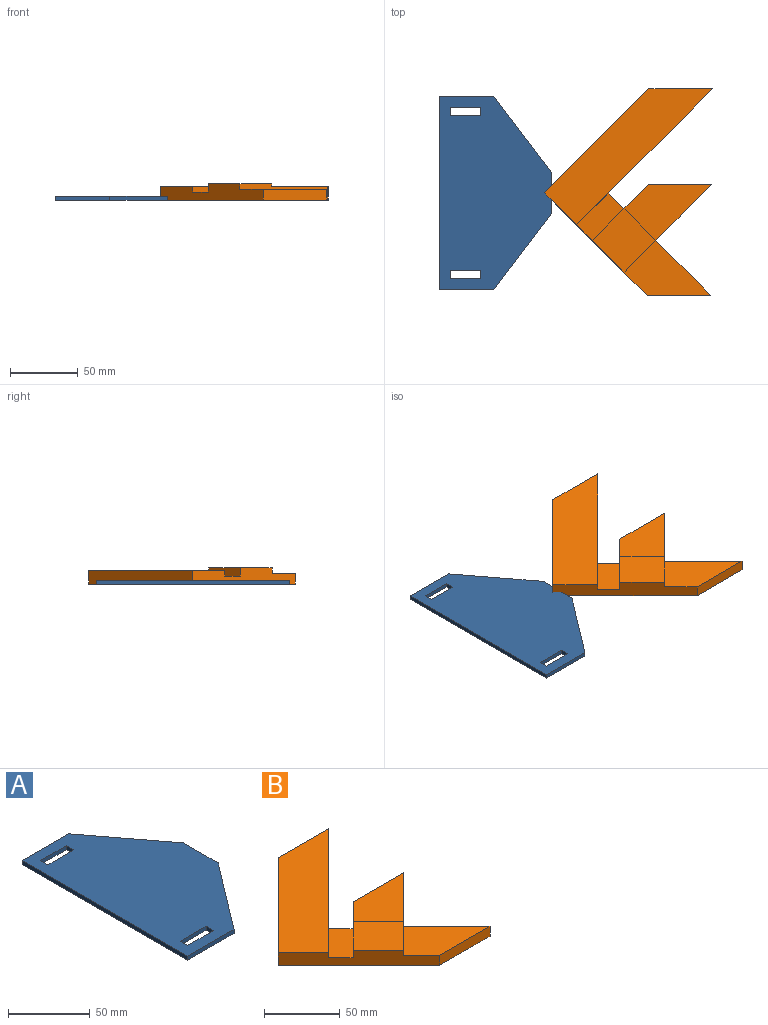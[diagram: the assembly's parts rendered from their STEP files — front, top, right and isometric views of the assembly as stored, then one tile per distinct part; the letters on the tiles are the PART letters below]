
ASSEMBLY  parts=2 mates=1
PART A: 16 faces, bbox 82.9x143x3 mm
  f0: plane 6.35x3mm, normal (-1,0,0), area 19mm2, adj f1,f13,f14,f15
  f1: plane 22.23x3mm, normal (0,1,0), area 66.7mm2, adj f0,f2,f14,f15
  f2: plane 6.35x3mm, normal (1,0,0), area 19mm2, adj f1,f13,f14,f15
  f3: plane 22.23x3mm, normal (0,-1,0), area 66.7mm2, adj f4,f11,f14,f15
  f4: plane 6.35x3mm, normal (-1,0,0), area 19mm2, adj f3,f5,f14,f15
  f5: plane 22.23x3mm, normal (0,1,0), area 66.7mm2, adj f4,f11,f14,f15
  f6: plane 40x3mm, normal (0,1,0), area 120mm2, adj f7,f12,f14,f15
  f7: plane 143x3mm, normal (-1,0,0), area 429mm2, adj f6,f8,f14,f15
  f8: plane 40x3mm, normal (0,-1,0), area 120mm2, adj f7,f9,f14,f15
  f9: plane 56.5x42.85mm, normal (0.8,-0.6,0), area 212.7mm2, adj f8,f10,f14,f15
  f10: plane 30x3mm, normal (1,0,0), area 90mm2, adj f9,f12,f14,f15
  f11: plane 6.35x3mm, normal (1,0,0), area 19mm2, adj f3,f5,f14,f15
  f12: plane 56.5x42.85mm, normal (0.8,0.6,0), area 212.7mm2, adj f6,f10,f14,f15
  f13: plane 22.23x3mm, normal (0,-1,0), area 66.7mm2, adj f0,f2,f14,f15
  f14: plane 143x82.85mm, normal (0,0,1), area 9144.3mm2, adj f0,f1,f2,f3,f4,f5,f6,f7
  f15: plane 143x82.85mm, normal (0,0,-1), area 9144.3mm2, adj f0,f1,f2,f3,f4,f5,f6,f7
PART B: 17 faces, bbox 123.9x152.5x12 mm
  f0: plane 100.42x100.42mm, normal (0.71,-0.71,0), area 1221.3mm2, adj f1,f3,f4,f14,f15,f16
  f1: plane 46.88x10mm, normal (0,1,0), area 468.8mm2, adj f0,f2,f4,f16
  f2: plane 76.98x76.98mm, normal (-0.71,0.71,0), area 1088.7mm2, adj f1,f3,f4,f16
  f3: plane 75.54x75.54mm, normal (-0.71,-0.71,0), area 1020.7mm2, adj f0,f2,f4,f5,f7,f8,f11,f12
  f4: plane 123.86x100.42mm, normal (0,0,1), area 4158.5mm2, adj f0,f1,f2,f3
  f5: plane 64.75x64.75mm, normal (0.71,-0.71,0), area 716.8mm2, adj f3,f6,f8,f9,f10,f12,f13,f16
  f6: plane 23.44x23.44mm, normal (0.71,0.71,0), area 66.3mm2, adj f5,f7,f8,f9
  f7: plane 41.31x41.31mm, normal (-0.71,0.71,0), area 451.6mm2, adj f3,f6,f8,f9,f10,f14,f15,f16
  f8: plane 46.88x46.88mm, normal (0,0,1), area 1098.9mm2, adj f3,f5,f6,f7
  f9: plane 64.75x41.31mm, normal (0,0,1), area 1387.3mm2, adj f5,f6,f7,f10
  f10: plane 46.88x10mm, normal (0,1,0), area 468.8mm2, adj f5,f7,f9,f16
  f11: plane 46.88x8mm, normal (0,-1,0), area 375mm2, adj f3,f12,f13,f16
  f12: plane 63.92x40.48mm, normal (0,0,1), area 1348.3mm2, adj f3,f5,f11,f13
  f13: plane 40.48x40.48mm, normal (0.71,0.71,0), area 458mm2, adj f5,f11,f12,f16
  f14: plane 11.62x11.62mm, normal (0.71,0.71,0), area 98.6mm2, adj f0,f7,f15,f16
  f15: plane 35.06x35.06mm, normal (0,0,1), area 544.7mm2, adj f0,f3,f7,f14
  f16: plane 152.52x123.86mm, normal (0,0,-1), area 8537.6mm2, adj f0,f1,f2,f3,f5,f7,f10,f11
PLACE A t=(-166.02,-50.67,-18.15)mm
PLACE B t=(44.17,16.95,-14.15)mm
MATE fastened B.f16 <-> A.f15  axis (0,0,-1) through (23.27,-18.7,-18.15)mm
